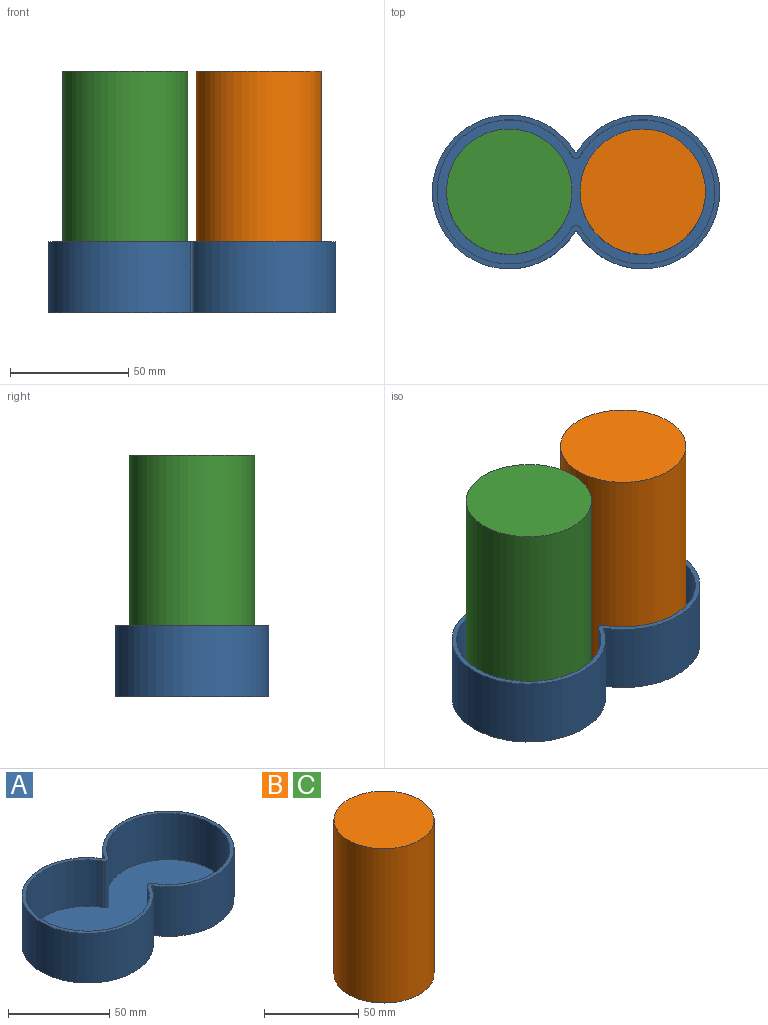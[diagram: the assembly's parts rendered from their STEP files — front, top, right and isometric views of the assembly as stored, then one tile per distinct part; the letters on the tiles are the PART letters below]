
ASSEMBLY  parts=3 mates=2
PART A: 11 faces, bbox 121.4x65x30 mm
  f0: plane 121.43x65mm, normal (0,0,1), area 669.7mm2, adj f1,f2,f4,f5,f7,f8,f9,f10
  f1: cylinder r=32.5mm len=65mm, axis (0,0,-1), area 5053.1mm2, adj f0,f3,f9,f10
  f2: cylinder r=32.5mm len=65mm, axis (0,0,-1), area 5053.1mm2, adj f0,f3,f9,f10
  f3: plane 121.43x65mm, normal (0,0,-1), area 6450.2mm2, adj f1,f2,f9,f10
  f4: cylinder r=30.5mm len=61mm, axis (0,0,-1), area 4478.8mm2, adj f0,f6,f7,f8
  f5: cylinder r=30.5mm len=61mm, axis (0,0,-1), area 4478.8mm2, adj f0,f6,f7,f8
  f6: plane 117.43x61mm, normal (0,0,1), area 5780.5mm2, adj f4,f5,f7,f8
  f7: cylinder r=2mm len=28mm, axis (0,0,-1), area 117.8mm2, adj f0,f4,f5,f6
  f8: cylinder r=2mm len=28mm, axis (0,0,-1), area 117.8mm2, adj f0,f4,f5,f6
  f9: cylinder r=0.6mm len=30mm, axis (0,0,1), area 36.7mm2, adj f0,f1,f2,f3
  f10: cylinder r=0.6mm len=30mm, axis (0,0,1), area 36.7mm2, adj f0,f1,f2,f3
PART B: 3 faces, bbox 53x53x100 mm
  f0: cylinder r=26.5mm len=100mm, axis (0,0,-1), area 16650.4mm2, adj f1,f2
  f1: plane 53x53mm, normal (0,0,1), area 2206.2mm2, adj f0
  f2: plane 53x53mm, normal (0,0,-1), area 2206.2mm2, adj f0
PART C: same geometry as B
PLACE A t=(-8.13,15.98,-4)mm fixed
PLACE B t=(56.43,0,0)mm
PLACE C at identity
MATE cylindrical B.f0 <-> A.f1  axis (0,0,-1) through (20.08,15.98,0)mm
MATE cylindrical A.f2 <-> C.f0  axis (0,0,1) through (-36.34,15.98,0)mm
